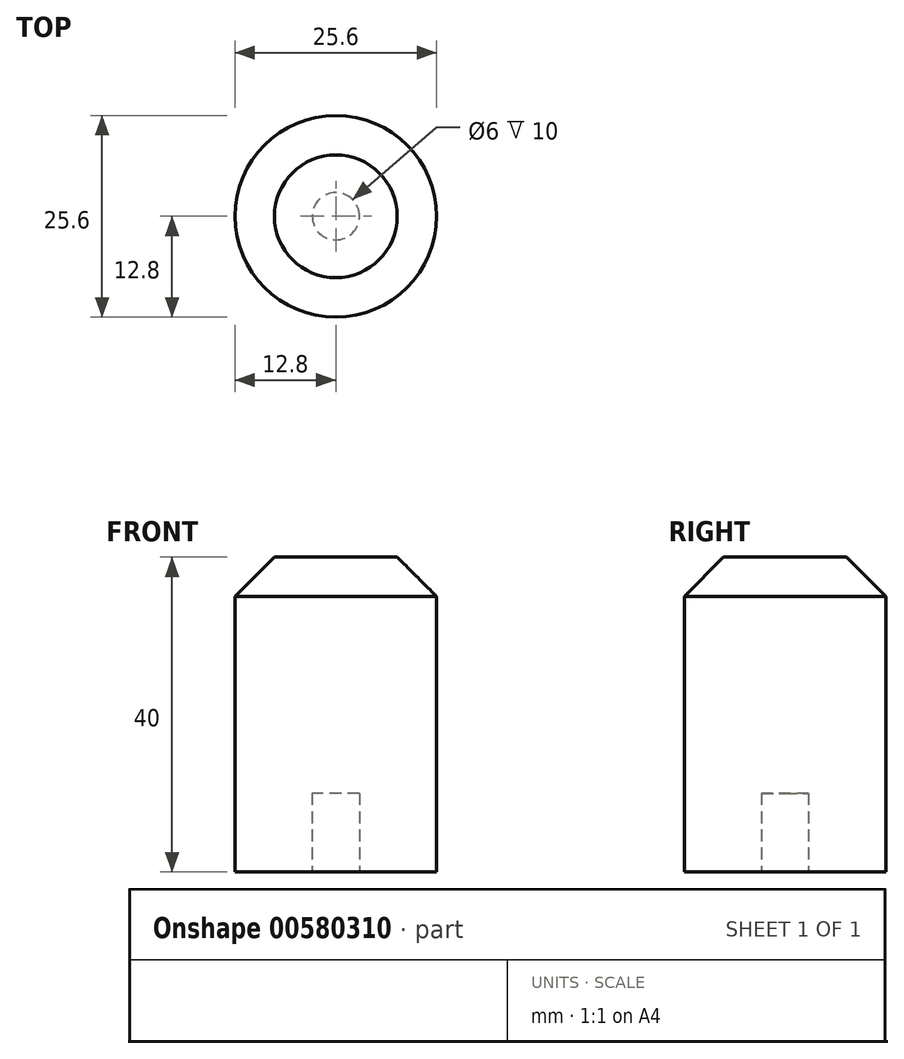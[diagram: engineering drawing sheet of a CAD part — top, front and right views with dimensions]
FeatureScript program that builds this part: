
annotation { "Feature Type Name" : "Feature", "Feature Type Description" : "" }
export const myFeature = defineFeature(function(context is Context, id is Id, definition is map)
    precondition{}
    {
        {
            var Q0;
            Q0=qCreatedBy(makeId("Top.planeOp"),FACE);
            var sketch = newSketch(context, id + "F0", { "sketchPlane" : qUnion([Q0])});
            skCircle(sketch, "E0", {"center": v(0, 0) * mm, "radius": 3 * mm});
            skCircle(sketch, "E1", {"center": v(0, 0) * mm, "radius": 12.8 * mm});
            skSolve(sketch);
        }
        {
            var Q0;
            Q0=makeQuery(id+"F0.imprint","IMPRINT",FACE,{"disambiguationData":[TD([[makeQuery(id+"F0.imprint","IMPRINT",EDGE,{"derivedFrom":sQuery(id+"F0.wireOp",EDGE,"E0")}),-1.0]])]});
            var Q1;
            Q1=makeQuery(id+"F0.imprint","IMPRINT",FACE,{"disambiguationData":[TD([[makeQuery(id+"F0.imprint","IMPRINT",EDGE,{"derivedFrom":sQuery(id+"F0.wireOp",EDGE,"E0")}),1.0]])]});
            extrude(context, id + "F1", {"entities" : qUnion([Q0, Q1]), "depth" : 40 * mm, "offsetDistance" : 25 * mm});
        }
        {
            var Q0;
            Q0=makeQuery(id+"F1.opExtrude","CAP_EDGE",EDGE,{"disambiguationData":[OSD([sQuery(id+"F0.wireOp",EDGE,"E1")])],"isStart":false});
            chamfer(context, id + "F2", {"entities" : qUnion([Q0]), "width" : 5 * mm, "tangentPropagation" : true});
        }
        {
            var Q0;
            Q0=makeQuery(id+"F0.imprint","IMPRINT",FACE,{"disambiguationData":[TD([[makeQuery(id+"F0.imprint","IMPRINT",EDGE,{"derivedFrom":sQuery(id+"F0.wireOp",EDGE,"E0")}),1.0]])]});
            extrude(context, id + "F3", {"entities" : qUnion([Q0]), "operationType" : NewBodyOperationType.REMOVE, "depth" : 10 * mm, "offsetDistance" : 25 * mm});
        }
    });
